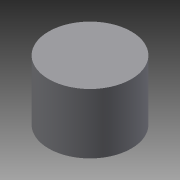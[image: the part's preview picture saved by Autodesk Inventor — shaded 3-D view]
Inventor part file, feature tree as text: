
AUTODESK INVENTOR PART (.ipt)
format: ipt  version: 2015 (Build 190159000, 159)  size: 74,240 bytes
history: native  units: in
note: dims shown in document units (in); Inventor stores cm internally (conversion verified against a paired STEP export)
features: extrude x2, sketch x2
ambient origin geometry x8: Origin, YZ Plane, XZ Plane, XY Plane, X Axis, Y Axis, Z Axis, Center Point
bodies: Solid1 (feature_tree)
feature tree (4):
  extrude  "Extrusion1"  Depth=4.0in TaperAngle=0.0deg
  extrude  "Extrusion2"  Depth=4.0in TaperAngle=0.0deg
  sketch  "Sketch1"  dims[d0=5.5in d1=4.0in d2=0.0in]
  sketch  "Sketch2"  dims[d3=0.125in d4=4.0in d5=0.0in]
